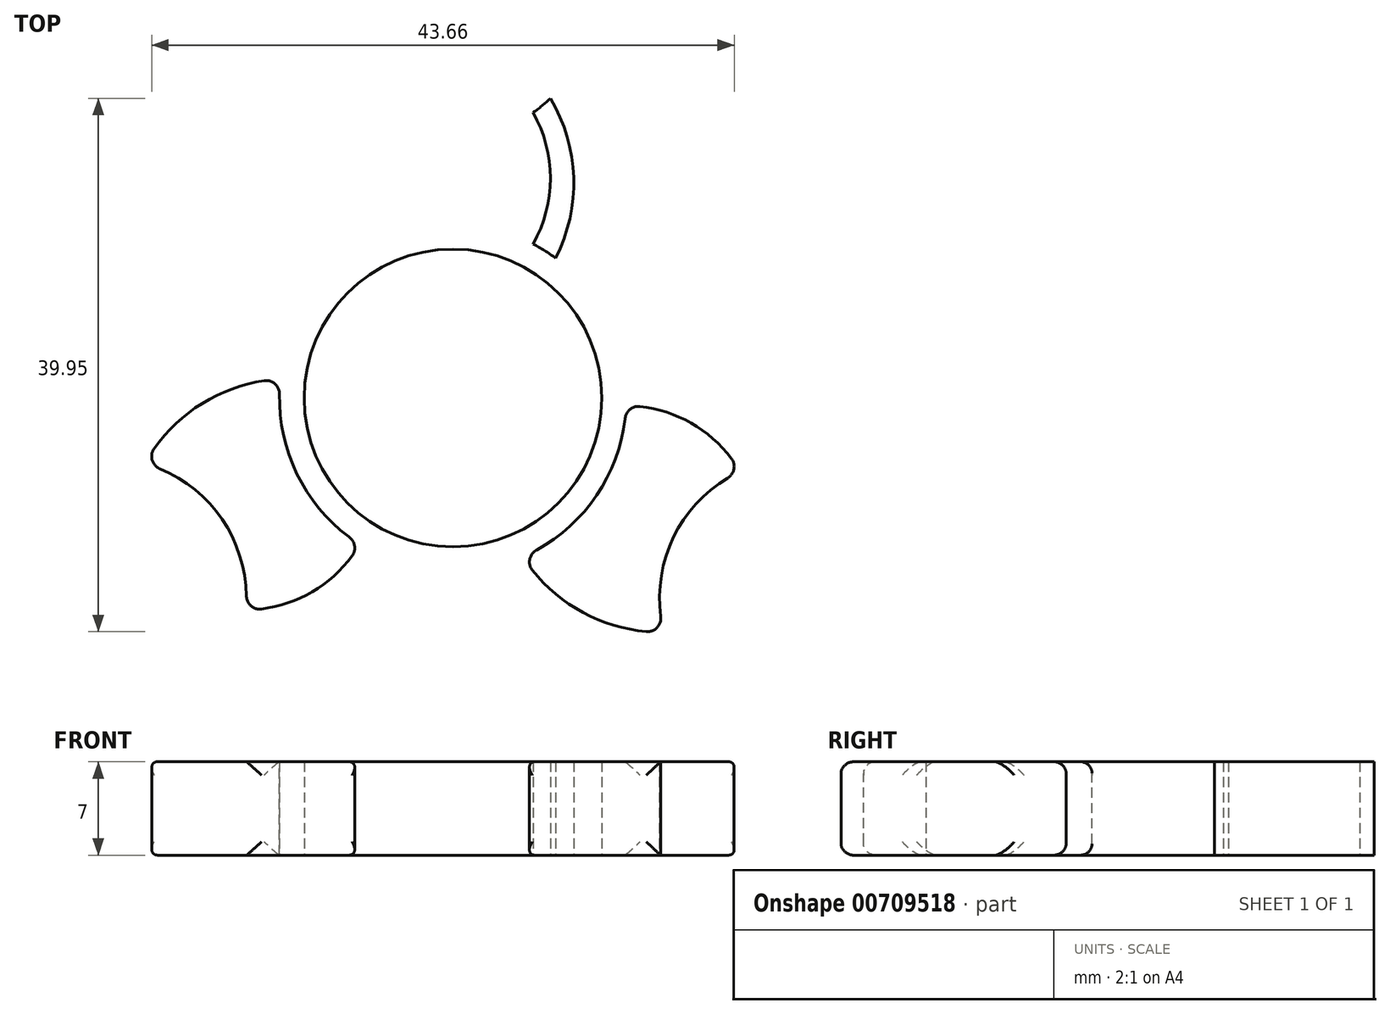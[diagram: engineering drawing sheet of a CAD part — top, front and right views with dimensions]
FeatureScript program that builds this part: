
annotation { "Feature Type Name" : "Feature", "Feature Type Description" : "" }
export const myFeature = defineFeature(function(context is Context, id is Id, definition is map)
    precondition{}
    {
        {
            var Q0;
            Q0=qCreatedBy(makeId("Top.planeOp"),FACE);
            var sketch = newSketch(context, id + "F0", { "sketchPlane" : qUnion([Q0])});
            skCircle(sketch, "E0", {"center": v(0, 0) * mm, "radius": 11.15 * mm});
            skCircle(sketch, "E1", {"center": v(0, 0) * mm, "radius": 13 * mm});
            skCircle(sketch, "E2.cCircle", {"center": v(0, 30) * mm, "radius": 8.5 * mm, "construction": true});
            skLineSegment(sketch, "E2.0", {"start": v(0, 38.5) * mm, "end": v(7.36, 34.25) * mm});
            skLineSegment(sketch, "E2.1", {"start": v(7.36, 34.25) * mm, "end": v(7.36, 25.75) * mm});
            skLineSegment(sketch, "E2.2", {"start": v(7.36, 25.75) * mm, "end": v(0, 21.5) * mm});
            skLineSegment(sketch, "E2.3", {"start": v(0, 21.5) * mm, "end": v(-7.36, 25.75) * mm});
            skLineSegment(sketch, "E2.4", {"start": v(-7.36, 25.75) * mm, "end": v(-7.36, 34.25) * mm});
            skLineSegment(sketch, "E2.5", {"start": v(-7.36, 34.25) * mm, "end": v(0, 38.5) * mm});
            skCircle(sketch, "E3", {"center": v(0, 30) * mm, "radius": 10.5 * mm});
            skArc(sketch, "E4", {"start": v(6, 11.53) * mm, "mid": v(7.3, 16.46) * mm, "end": v(6, 21.38) * mm});
            skArc(sketch, "E5", {"start": v(7.69, 10.48) * mm, "mid": v(9.04, 16.52) * mm, "end": v(7.3, 22.45) * mm});
            skPoint(sketch, "E5.endSnap0", {"position": v(7.3, 16.46) * mm});
            skArc(sketch, "E6.MirrorCS", {"start": v(-7.69, 10.48) * mm, "mid": v(-9.04, 16.52) * mm, "end": v(-7.3, 22.45) * mm});
            skPoint(sketch, "E7.MirrorP", {"position": v(-7.3, 16.46) * mm});
            skArc(sketch, "E8.MirrorCS", {"start": v(-6, 11.53) * mm, "mid": v(-7.3, 16.46) * mm, "end": v(-6, 21.38) * mm});
            skLineSegment(sketch, "E9.MirrorCS", {"start": v(0, 38.5) * mm, "end": v(-7.36, 34.25) * mm});
            skLineSegment(sketch, "E10.MirrorCS", {"start": v(-7.36, 34.25) * mm, "end": v(-7.36, 25.75) * mm});
            skLineSegment(sketch, "E11.MirrorCS", {"start": v(-7.36, 25.75) * mm, "end": v(0, 21.5) * mm});
            skLineSegment(sketch, "E12.MirrorCS", {"start": v(0, 21.5) * mm, "end": v(7.36, 25.75) * mm});
            skLineSegment(sketch, "E13.MirrorCS", {"start": v(7.36, 25.75) * mm, "end": v(7.36, 34.25) * mm});
            skLineSegment(sketch, "E14.MirrorCS", {"start": v(7.36, 34.25) * mm, "end": v(0, 38.5) * mm});
            skPoint(sketch, "E15.1.0", {"position": v(-10.6, -14.55) * mm});
            skArc(sketch, "E15.1.1", {"start": v(-6.99, -10.96) * mm, "mid": v(-10.6, -14.55) * mm, "end": v(-15.52, -15.89) * mm});
            skPoint(sketch, "E15.1.2", {"position": v(-17.9, -1.9) * mm});
            skLineSegment(sketch, "E15.1.5", {"start": v(-33.34, -10.75) * mm, "end": v(-25.98, -6.5) * mm});
            skLineSegment(sketch, "E15.1.6", {"start": v(-18.62, -10.75) * mm, "end": v(-18.62, -19.25) * mm});
            skLineSegment(sketch, "E15.1.7", {"start": v(-25.98, -23.5) * mm, "end": v(-33.34, -19.25) * mm});
            skArc(sketch, "E15.1.8", {"start": v(-12.99, -0.57) * mm, "mid": v(-17.9, -1.9) * mm, "end": v(-21.52, -5.5) * mm});
            skArc(sketch, "E15.1.9", {"start": v(-12.92, 1.42) * mm, "mid": v(-18.83, -0.43) * mm, "end": v(-23.1, -4.9) * mm});
            skArc(sketch, "E15.1.10", {"start": v(-5.23, -11.9) * mm, "mid": v(-9.78, -16.1) * mm, "end": v(-15.8, -17.54) * mm});
            skCircle(sketch, "E15.1.11", {"center": v(-25.98, -15) * mm, "radius": 10.5 * mm});
            skLineSegment(sketch, "E15.1.12", {"start": v(-33.34, -10.75) * mm, "end": v(-33.34, -19.25) * mm});
            skLineSegment(sketch, "E15.1.13", {"start": v(-18.62, -10.75) * mm, "end": v(-25.98, -6.5) * mm});
            skLineSegment(sketch, "E15.1.14", {"start": v(-25.98, -23.5) * mm, "end": v(-18.62, -19.25) * mm});
            skCircle(sketch, "E15.1.15", {"center": v(-25.98, -15) * mm, "radius": 8.5 * mm, "construction": true});
            skLineSegment(sketch, "E15.1.16", {"start": v(-25.98, -6.5) * mm, "end": v(-33.34, -10.75) * mm});
            skLineSegment(sketch, "E15.1.17", {"start": v(-18.62, -19.25) * mm, "end": v(-18.62, -10.75) * mm});
            skLineSegment(sketch, "E15.1.18", {"start": v(-33.34, -19.25) * mm, "end": v(-25.98, -23.5) * mm});
            skLineSegment(sketch, "E15.1.20", {"start": v(-33.34, -19.25) * mm, "end": v(-33.34, -10.75) * mm});
            skCircle(sketch, "E15.1.22", {"center": v(-25.98, -15) * mm, "radius": 8.5 * mm, "construction": true});
            skLineSegment(sketch, "E15.1.23", {"start": v(-25.98, -6.5) * mm, "end": v(-18.62, -10.75) * mm});
            skLineSegment(sketch, "E15.1.24", {"start": v(-18.62, -19.25) * mm, "end": v(-25.98, -23.5) * mm});
            skCircle(sketch, "E15.1.25", {"center": v(-25.98, -15) * mm, "radius": 10.5 * mm});
            skPoint(sketch, "E15.2.0", {"position": v(17.9, -1.9) * mm});
            skArc(sketch, "E15.2.1", {"start": v(12.99, -0.57) * mm, "mid": v(17.9, -1.9) * mm, "end": v(21.52, -5.5) * mm});
            skPoint(sketch, "E15.2.2", {"position": v(10.6, -14.55) * mm});
            skLineSegment(sketch, "E15.2.5", {"start": v(25.98, -23.5) * mm, "end": v(18.62, -19.25) * mm});
            skLineSegment(sketch, "E15.2.6", {"start": v(18.62, -10.75) * mm, "end": v(25.98, -6.5) * mm});
            skLineSegment(sketch, "E15.2.7", {"start": v(33.34, -10.75) * mm, "end": v(33.34, -19.25) * mm});
            skArc(sketch, "E15.2.8", {"start": v(6.99, -10.96) * mm, "mid": v(10.6, -14.55) * mm, "end": v(15.52, -15.89) * mm});
            skArc(sketch, "E15.2.9", {"start": v(5.23, -11.9) * mm, "mid": v(9.78, -16.1) * mm, "end": v(15.8, -17.54) * mm});
            skArc(sketch, "E15.2.10", {"start": v(12.92, 1.42) * mm, "mid": v(18.83, -0.43) * mm, "end": v(23.1, -4.9) * mm});
            skCircle(sketch, "E15.2.11", {"center": v(25.98, -15) * mm, "radius": 10.5 * mm});
            skLineSegment(sketch, "E15.2.12", {"start": v(25.98, -23.5) * mm, "end": v(33.34, -19.25) * mm});
            skLineSegment(sketch, "E15.2.13", {"start": v(18.62, -10.75) * mm, "end": v(18.62, -19.25) * mm});
            skLineSegment(sketch, "E15.2.14", {"start": v(33.34, -10.75) * mm, "end": v(25.98, -6.5) * mm});
            skCircle(sketch, "E15.2.15", {"center": v(25.98, -15) * mm, "radius": 8.5 * mm, "construction": true});
            skLineSegment(sketch, "E15.2.16", {"start": v(18.62, -19.25) * mm, "end": v(25.98, -23.5) * mm});
            skLineSegment(sketch, "E15.2.17", {"start": v(25.98, -6.5) * mm, "end": v(18.62, -10.75) * mm});
            skLineSegment(sketch, "E15.2.18", {"start": v(33.34, -19.25) * mm, "end": v(33.34, -10.75) * mm});
            skLineSegment(sketch, "E15.2.20", {"start": v(33.34, -19.25) * mm, "end": v(25.98, -23.5) * mm});
            skCircle(sketch, "E15.2.22", {"center": v(25.98, -15) * mm, "radius": 8.5 * mm, "construction": true});
            skLineSegment(sketch, "E15.2.23", {"start": v(18.62, -19.25) * mm, "end": v(18.62, -10.75) * mm});
            skLineSegment(sketch, "E15.2.24", {"start": v(25.98, -6.5) * mm, "end": v(33.34, -10.75) * mm});
            skCircle(sketch, "E15.2.25", {"center": v(25.98, -15) * mm, "radius": 10.5 * mm});
            skSolve(sketch);
        }
        {
            var Q0;
            Q0=makeQuery(id+"F0.imprint","IMPRINT",FACE,{"disambiguationData":[TD([[makeQuery(id+"F0.imprint","IMPRINT",EDGE,{"derivedFrom":sQuery(id+"F0.wireOp",EDGE,"E15.1.16")}),-1.0]])]});
            var Q1;
            {var subQ0=sQuery(id+"F0.wireOp",EDGE,"E15.1.8");Q1=makeQuery(id+"F0.imprint","IMPRINT",FACE,{"disambiguationData":[TD([[makeQuery(id+"F0.imprint","IMPRINT",EDGE,{"derivedFrom":subQ0}),-1.0]])]});}
            var Q2;
            {var subQ0=sQuery(id+"F0.wireOp",EDGE,"E15.1.1");Q2=makeQuery(id+"F0.imprint","IMPRINT",FACE,{"disambiguationData":[TD([[makeQuery(id+"F0.imprint","IMPRINT",EDGE,{"derivedFrom":subQ0}),1.0]])]});}
            var Q3;
            Q3=makeQuery(id+"F0.imprint","IMPRINT",FACE,{"disambiguationData":[TD([[makeQuery(id+"F0.imprint","IMPRINT",EDGE,{"derivedFrom":sQuery(id+"F0.wireOp",EDGE,"E0")}),1.0]])]});
            var Q4;
            {var subQ0=sQuery(id+"F0.wireOp",EDGE,"E6.MirrorCS");Q4=makeQuery(id+"F0.imprint","IMPRINT",FACE,{"disambiguationData":[TD([[makeQuery(id+"F0.imprint","IMPRINT",EDGE,{"derivedFrom":subQ0}),-1.0]])]});}
            var Q5;
            Q5=makeQuery(id+"F0.imprint","IMPRINT",FACE,{"disambiguationData":[TD([[makeQuery(id+"F0.imprint","IMPRINT",EDGE,{"derivedFrom":sQuery(id+"F0.wireOp",EDGE,"E9.MirrorCS")}),-1.0]])]});
            var Q6;
            {var subQ0=sQuery(id+"F0.wireOp",EDGE,"E4");Q6=makeQuery(id+"F0.imprint","IMPRINT",FACE,{"disambiguationData":[TD([[makeQuery(id+"F0.imprint","IMPRINT",EDGE,{"derivedFrom":subQ0}),-1.0]])]});}
            var Q7;
            {var subQ0=sQuery(id+"F0.wireOp",EDGE,"E15.2.1");Q7=makeQuery(id+"F0.imprint","IMPRINT",FACE,{"disambiguationData":[TD([[makeQuery(id+"F0.imprint","IMPRINT",EDGE,{"derivedFrom":subQ0}),1.0]])]});}
            var Q8;
            {var subQ0=sQuery(id+"F0.wireOp",EDGE,"E15.2.8");Q8=makeQuery(id+"F0.imprint","IMPRINT",FACE,{"disambiguationData":[TD([[makeQuery(id+"F0.imprint","IMPRINT",EDGE,{"derivedFrom":subQ0}),-1.0]])]});}
            var Q9;
            Q9=makeQuery(id+"F0.imprint","IMPRINT",FACE,{"disambiguationData":[TD([[makeQuery(id+"F0.imprint","IMPRINT",EDGE,{"derivedFrom":sQuery(id+"F0.wireOp",EDGE,"E15.2.16")}),-1.0]])]});
            extrude(context, id + "F1", {"entities" : qUnion([Q0, Q1, Q2, Q3, Q4, Q5, Q6, Q7, Q8, Q9]), "depth" : 7 * mm, "offsetDistance" : 25 * mm});
        }
        {
            var Q0;
            Q0=makeQuery(id+"F1.opExtrude","SWEPT_FACE",FACE,{"disambiguationData":[OSD([sQuery(id+"F0.wireOp",EDGE,"E15.1.10")])]});
            var Q1;
            Q1=makeQuery(id+"F1.opExtrude","SWEPT_FACE",FACE,{"disambiguationData":[OSD([sQuery(id+"F0.wireOp",EDGE,"E15.1.9")])]});
            var Q2;
            Q2=makeQuery(id+"F1.opExtrude","SWEPT_FACE",FACE,{"disambiguationData":[OSD([sQuery(id+"F0.wireOp",EDGE,"E6.MirrorCS")])]});
            var Q3;
            Q3=makeQuery(id+"F1.opExtrude","SWEPT_FACE",FACE,{"disambiguationData":[OSD([sQuery(id+"F0.wireOp",EDGE,"E5")])]});
            var Q4;
            Q4=makeQuery(id+"F1.opExtrude","SWEPT_FACE",FACE,{"disambiguationData":[OSD([sQuery(id+"F0.wireOp",EDGE,"E15.2.10")])]});
            var Q5;
            Q5=makeQuery(id+"F1.opExtrude","SWEPT_FACE",FACE,{"disambiguationData":[OSD([sQuery(id+"F0.wireOp",EDGE,"E15.2.9")])]});
            var Q6;
            Q6=makeQuery(id+"F1.opExtrude","SWEPT_FACE",FACE,{"disambiguationData":[OSD([sQuery(id+"F0.wireOp",EDGE,"E15.2.1")])]});
            var Q7;
            Q7=makeQuery(id+"F1.opExtrude","SWEPT_FACE",FACE,{"disambiguationData":[OSD([sQuery(id+"F0.wireOp",EDGE,"E15.2.8")])]});
            var Q8;
            Q8=makeQuery(id+"F1.opExtrude","CAP_EDGE",EDGE,{"disambiguationData":[OSD([sQuery(id+"F0.wireOp",EDGE,"E4")])],"isStart":true});
            var Q9;
            Q9=makeQuery(id+"F1.opExtrude","SWEPT_FACE",FACE,{"disambiguationData":[OSD([sQuery(id+"F0.wireOp",EDGE,"E8.MirrorCS")])]});
            var Q10;
            Q10=makeQuery(id+"F1.opExtrude","SWEPT_FACE",FACE,{"disambiguationData":[OSD([sQuery(id+"F0.wireOp",EDGE,"E15.1.1")])]});
            var Q11;
            Q11=makeQuery(id+"F1.opExtrude","SWEPT_FACE",FACE,{"disambiguationData":[OSD([sQuery(id+"F0.wireOp",EDGE,"E15.1.8")])]});
            var Q12;
            Q12=makeQuery(id+"F1.opExtrude","SWEPT_FACE",FACE,{"disambiguationData":[OSD([sQuery(id+"F0.wireOp",EDGE,"E4")])]});
            fillet(context, id + "F2", {"entities" : qUnion([Q0, Q1, Q2, Q3, Q4, Q5, Q6, Q7, Q8, Q9, Q10, Q11, Q12]), "radius" : 1 * mm, "tangentPropagation" : true, "allowEdgeOverflow" : false});
        }
    });
